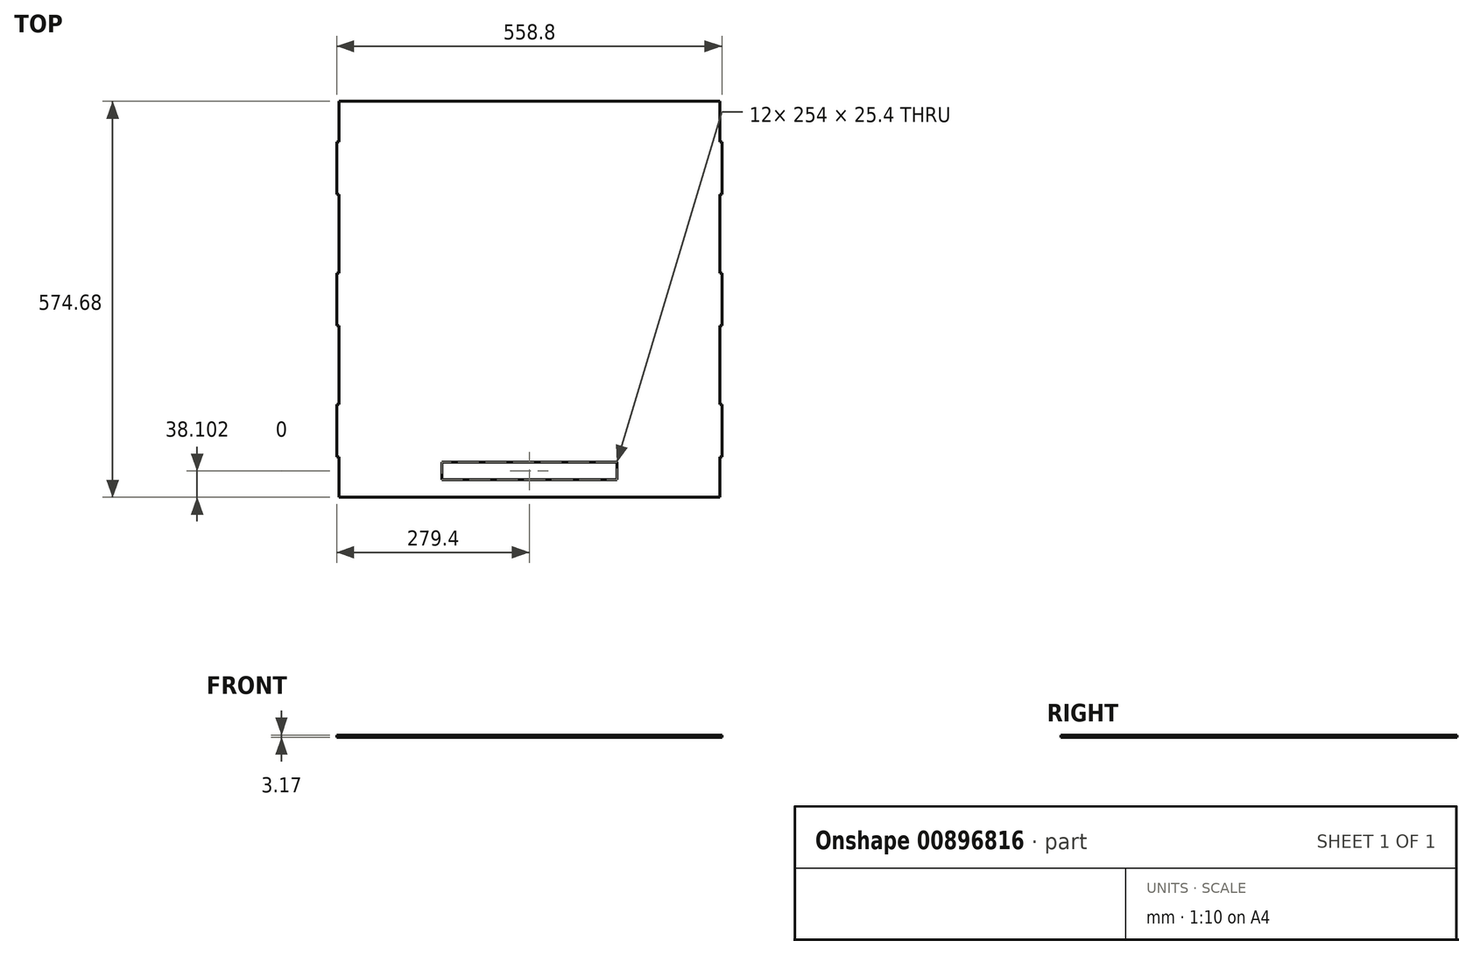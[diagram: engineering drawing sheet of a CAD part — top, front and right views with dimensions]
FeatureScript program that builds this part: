
annotation { "Feature Type Name" : "Feature", "Feature Type Description" : "" }
export const myFeature = defineFeature(function(context is Context, id is Id, definition is map)
    precondition{}
    {
        {
            var Q0;
            Q0=qCreatedBy(makeId("Top.planeOp"),FACE);
            var sketch = newSketch(context, id + "F0", { "sketchPlane" : qUnion([Q0])});
            skLineSegment(sketch, "E0.bottom", {"start": v(276.23, -287.34) * mm, "end": v(-276.23, -287.34) * mm});
            skLineSegment(sketch, "E0.top", {"start": v(276.23, 287.34) * mm, "end": v(-276.23, 287.34) * mm});
            skLineSegment(sketch, "E0.left", {"start": v(276.23, -287.34) * mm, "end": v(276.23, -228.6) * mm});
            skLineSegment(sketch, "E0.right", {"start": v(-276.23, -287.34) * mm, "end": v(-276.23, -228.6) * mm});
            skPoint(sketch, "E0.middle", {"position": v(0, 0) * mm});
            skLineSegment(sketch, "E1", {"start": v(0, 0) * mm, "end": v(441.24, 0) * mm, "construction": true});
            skLineSegment(sketch, "E2.bottom", {"start": v(276.23, 38.1) * mm, "end": v(279.4, 38.1) * mm});
            skLineSegment(sketch, "E2.top", {"start": v(276.23, -38.1) * mm, "end": v(279.4, -38.1) * mm});
            skLineSegment(sketch, "E2.right", {"start": v(279.4, 38.1) * mm, "end": v(279.4, -38.1) * mm});
            skLineSegment(sketch, "E3.bottom", {"start": v(279.4, 152.4) * mm, "end": v(276.22, 152.4) * mm});
            skLineSegment(sketch, "E3.top", {"start": v(279.4, 228.6) * mm, "end": v(276.22, 228.6) * mm});
            skLineSegment(sketch, "E3.left", {"start": v(279.4, 152.4) * mm, "end": v(279.4, 228.6) * mm});
            skLineSegment(sketch, "E4.bottom", {"start": v(279.4, -152.4) * mm, "end": v(276.23, -152.4) * mm});
            skLineSegment(sketch, "E4.top", {"start": v(279.4, -228.6) * mm, "end": v(276.23, -228.6) * mm});
            skLineSegment(sketch, "E4.left", {"start": v(279.4, -152.4) * mm, "end": v(279.4, -228.6) * mm});
            skLineSegment(sketch, "E5.trimOffspring", {"start": v(276.23, 228.6) * mm, "end": v(276.23, 287.34) * mm});
            skLineSegment(sketch, "E6.trimOffspring", {"start": v(276.23, 38.1) * mm, "end": v(276.23, 152.4) * mm});
            skLineSegment(sketch, "E7.trimOffspring", {"start": v(276.23, -152.4) * mm, "end": v(276.23, -38.1) * mm});
            skLineSegment(sketch, "E8", {"start": v(276.22, 228.6) * mm, "end": v(-297.73, 228.6) * mm, "construction": true});
            skLineSegment(sketch, "E9", {"start": v(276.22, 152.4) * mm, "end": v(-297.25, 152.4) * mm, "construction": true});
            skLineSegment(sketch, "E10", {"start": v(276.23, 38.1) * mm, "end": v(-290.5, 38.1) * mm, "construction": true});
            skLineSegment(sketch, "E11", {"start": v(276.23, -38.1) * mm, "end": v(-313.15, -38.1) * mm, "construction": true});
            skLineSegment(sketch, "E12", {"start": v(279.4, -152.4) * mm, "end": v(-294.35, -152.4) * mm, "construction": true});
            skLineSegment(sketch, "E13", {"start": v(276.23, -228.6) * mm, "end": v(-301.1, -228.6) * mm, "construction": true});
            skLineSegment(sketch, "E14.bottom", {"start": v(-279.4, 228.6) * mm, "end": v(-276.23, 228.6) * mm});
            skLineSegment(sketch, "E14.top", {"start": v(-279.4, 152.4) * mm, "end": v(-276.23, 152.4) * mm});
            skLineSegment(sketch, "E14.left", {"start": v(-279.4, 228.6) * mm, "end": v(-279.4, 152.4) * mm});
            skLineSegment(sketch, "E15.bottom", {"start": v(-279.4, 38.1) * mm, "end": v(-276.23, 38.1) * mm});
            skLineSegment(sketch, "E15.top", {"start": v(-279.4, -38.1) * mm, "end": v(-276.23, -38.1) * mm});
            skLineSegment(sketch, "E15.left", {"start": v(-279.4, 38.1) * mm, "end": v(-279.4, -38.1) * mm});
            skLineSegment(sketch, "E16.bottom", {"start": v(-279.4, -152.4) * mm, "end": v(-276.23, -152.4) * mm});
            skLineSegment(sketch, "E16.top", {"start": v(-279.4, -228.6) * mm, "end": v(-276.23, -228.6) * mm});
            skLineSegment(sketch, "E16.left", {"start": v(-279.4, -152.4) * mm, "end": v(-279.4, -228.6) * mm});
            skLineSegment(sketch, "E17.trimOffspring", {"start": v(-276.23, -152.4) * mm, "end": v(-276.23, -38.1) * mm});
            skLineSegment(sketch, "E18.trimOffspring", {"start": v(-276.23, 38.1) * mm, "end": v(-276.23, 152.4) * mm});
            skLineSegment(sketch, "E19.trimOffspring", {"start": v(-276.23, 228.6) * mm, "end": v(-276.23, 287.34) * mm});
            skSolve(sketch);
        }
        {
            var Q0;
            Q0 = qSketchRegion(id + "F0", true);
            extrude(context, id + "F1", {"entities" : qUnion([Q0]), "depth" : 3.17 * mm, "offsetDistance" : 25.4 * mm});
        }
        {
            var Q0;
            Q0=makeQuery(id+"F1.opExtrude","CAP_FACE",FACE,{"disambiguationData":[OSD([sQuery(id+"F0.wireOp",EDGE,"E0.bottom"),sQuery(id+"F0.wireOp",EDGE,"E0.top"),sQuery(id+"F0.wireOp",EDGE,"E0.left"),sQuery(id+"F0.wireOp",EDGE,"E0.right"),sQuery(id+"F0.wireOp",EDGE,"E2.bottom"),sQuery(id+"F0.wireOp",EDGE,"E2.top"),sQuery(id+"F0.wireOp",EDGE,"E2.right"),sQuery(id+"F0.wireOp",EDGE,"E3.bottom"),sQuery(id+"F0.wireOp",EDGE,"E3.top"),sQuery(id+"F0.wireOp",EDGE,"E3.left"),sQuery(id+"F0.wireOp",EDGE,"E4.bottom"),sQuery(id+"F0.wireOp",EDGE,"E4.top"),sQuery(id+"F0.wireOp",EDGE,"E4.left"),sQuery(id+"F0.wireOp",EDGE,"E5.trimOffspring"),sQuery(id+"F0.wireOp",EDGE,"E6.trimOffspring"),sQuery(id+"F0.wireOp",EDGE,"E7.trimOffspring"),sQuery(id+"F0.wireOp",EDGE,"E14.bottom"),sQuery(id+"F0.wireOp",EDGE,"E14.top"),sQuery(id+"F0.wireOp",EDGE,"E14.left"),sQuery(id+"F0.wireOp",EDGE,"E15.bottom"),sQuery(id+"F0.wireOp",EDGE,"E15.top"),sQuery(id+"F0.wireOp",EDGE,"E15.left"),sQuery(id+"F0.wireOp",EDGE,"E16.bottom"),sQuery(id+"F0.wireOp",EDGE,"E16.top"),sQuery(id+"F0.wireOp",EDGE,"E16.left"),sQuery(id+"F0.wireOp",EDGE,"E17.trimOffspring"),sQuery(id+"F0.wireOp",EDGE,"E18.trimOffspring"),sQuery(id+"F0.wireOp",EDGE,"E19.trimOffspring")])],"isStart":false});
            var sketch = newSketch(context, id + "F2", { "sketchPlane" : qUnion([Q0])});
            skLineSegment(sketch, "E20.0.0", {"start": v(276.23, 228.6) * mm, "end": v(276.23, 287.34) * mm, "construction": true});
            skLineSegment(sketch, "E20.0.1", {"start": v(276.23, 287.34) * mm, "end": v(-276.23, 287.34) * mm, "construction": true});
            skLineSegment(sketch, "E20.0.2", {"start": v(-276.23, 287.34) * mm, "end": v(-276.23, 228.6) * mm, "construction": true});
            skLineSegment(sketch, "E20.0.3", {"start": v(-276.23, 228.6) * mm, "end": v(-279.4, 228.6) * mm, "construction": true});
            skLineSegment(sketch, "E20.0.4", {"start": v(-279.4, 228.6) * mm, "end": v(-279.4, 152.4) * mm, "construction": true});
            skLineSegment(sketch, "E20.0.5", {"start": v(-279.4, 152.4) * mm, "end": v(-276.23, 152.4) * mm, "construction": true});
            skLineSegment(sketch, "E20.0.6", {"start": v(-276.23, 152.4) * mm, "end": v(-276.23, 38.1) * mm, "construction": true});
            skLineSegment(sketch, "E20.0.7", {"start": v(-276.23, 38.1) * mm, "end": v(-279.4, 38.1) * mm, "construction": true});
            skLineSegment(sketch, "E20.0.8", {"start": v(-279.4, 38.1) * mm, "end": v(-279.4, -38.1) * mm, "construction": true});
            skLineSegment(sketch, "E20.0.9", {"start": v(-279.4, -38.1) * mm, "end": v(-276.23, -38.1) * mm, "construction": true});
            skLineSegment(sketch, "E20.0.10", {"start": v(-276.23, -38.1) * mm, "end": v(-276.23, -152.4) * mm, "construction": true});
            skLineSegment(sketch, "E20.0.11", {"start": v(-276.23, -152.4) * mm, "end": v(-279.4, -152.4) * mm, "construction": true});
            skLineSegment(sketch, "E20.0.12", {"start": v(-279.4, -152.4) * mm, "end": v(-279.4, -228.6) * mm, "construction": true});
            skLineSegment(sketch, "E20.0.13", {"start": v(-279.4, -228.6) * mm, "end": v(-276.23, -228.6) * mm, "construction": true});
            skLineSegment(sketch, "E20.0.14", {"start": v(-276.23, -228.6) * mm, "end": v(-276.23, -287.34) * mm, "construction": true});
            skLineSegment(sketch, "E20.0.15", {"start": v(-276.23, -287.34) * mm, "end": v(276.23, -287.34) * mm, "construction": true});
            skLineSegment(sketch, "E20.0.16", {"start": v(276.23, -287.34) * mm, "end": v(276.23, -228.6) * mm, "construction": true});
            skLineSegment(sketch, "E20.0.17", {"start": v(276.23, -228.6) * mm, "end": v(279.4, -228.6) * mm, "construction": true});
            skLineSegment(sketch, "E20.0.18", {"start": v(279.4, -228.6) * mm, "end": v(279.4, -152.4) * mm, "construction": true});
            skLineSegment(sketch, "E20.0.19", {"start": v(279.4, -152.4) * mm, "end": v(276.23, -152.4) * mm, "construction": true});
            skLineSegment(sketch, "E20.0.20", {"start": v(276.23, -152.4) * mm, "end": v(276.23, -38.1) * mm, "construction": true});
            skLineSegment(sketch, "E20.0.21", {"start": v(276.23, -38.1) * mm, "end": v(279.4, -38.1) * mm, "construction": true});
            skLineSegment(sketch, "E20.0.22", {"start": v(279.4, -38.1) * mm, "end": v(279.4, 38.1) * mm, "construction": true});
            skLineSegment(sketch, "E20.0.23", {"start": v(279.4, 38.1) * mm, "end": v(276.23, 38.1) * mm, "construction": true});
            skLineSegment(sketch, "E20.0.24", {"start": v(276.23, 38.1) * mm, "end": v(276.23, 152.4) * mm, "construction": true});
            skLineSegment(sketch, "E20.0.25", {"start": v(276.23, 152.4) * mm, "end": v(279.4, 152.4) * mm, "construction": true});
            skLineSegment(sketch, "E20.0.26", {"start": v(279.4, 152.4) * mm, "end": v(279.4, 228.6) * mm, "construction": true});
            skLineSegment(sketch, "E20.0.27", {"start": v(279.4, 228.6) * mm, "end": v(276.22, 228.6) * mm, "construction": true});
            skLineSegment(sketch, "E21", {"start": v(0, 0) * mm, "end": v(0, -287.34) * mm, "construction": true});
            skLineSegment(sketch, "E22.bottom", {"start": v(127, -236.54) * mm, "end": v(-127, -236.54) * mm});
            skLineSegment(sketch, "E22.top", {"start": v(127, -261.94) * mm, "end": v(-127, -261.94) * mm});
            skLineSegment(sketch, "E22.left", {"start": v(127, -236.54) * mm, "end": v(127, -261.94) * mm});
            skLineSegment(sketch, "E22.right", {"start": v(-127, -236.54) * mm, "end": v(-127, -261.94) * mm});
            skPoint(sketch, "E22.middle", {"position": v(0, -249.24) * mm});
            skSolve(sketch);
        }
        {
            var Q0;
            Q0 = qSketchRegion(id + "F2", true);
            extrude(context, id + "F3", {"entities" : qUnion([Q0]), "operationType" : NewBodyOperationType.REMOVE, "endBound" : BoundingType.THROUGH_ALL, "oppositeDirection" : true, "depth" : 25.4 * mm, "offsetDistance" : 25.4 * mm});
        }
    });
